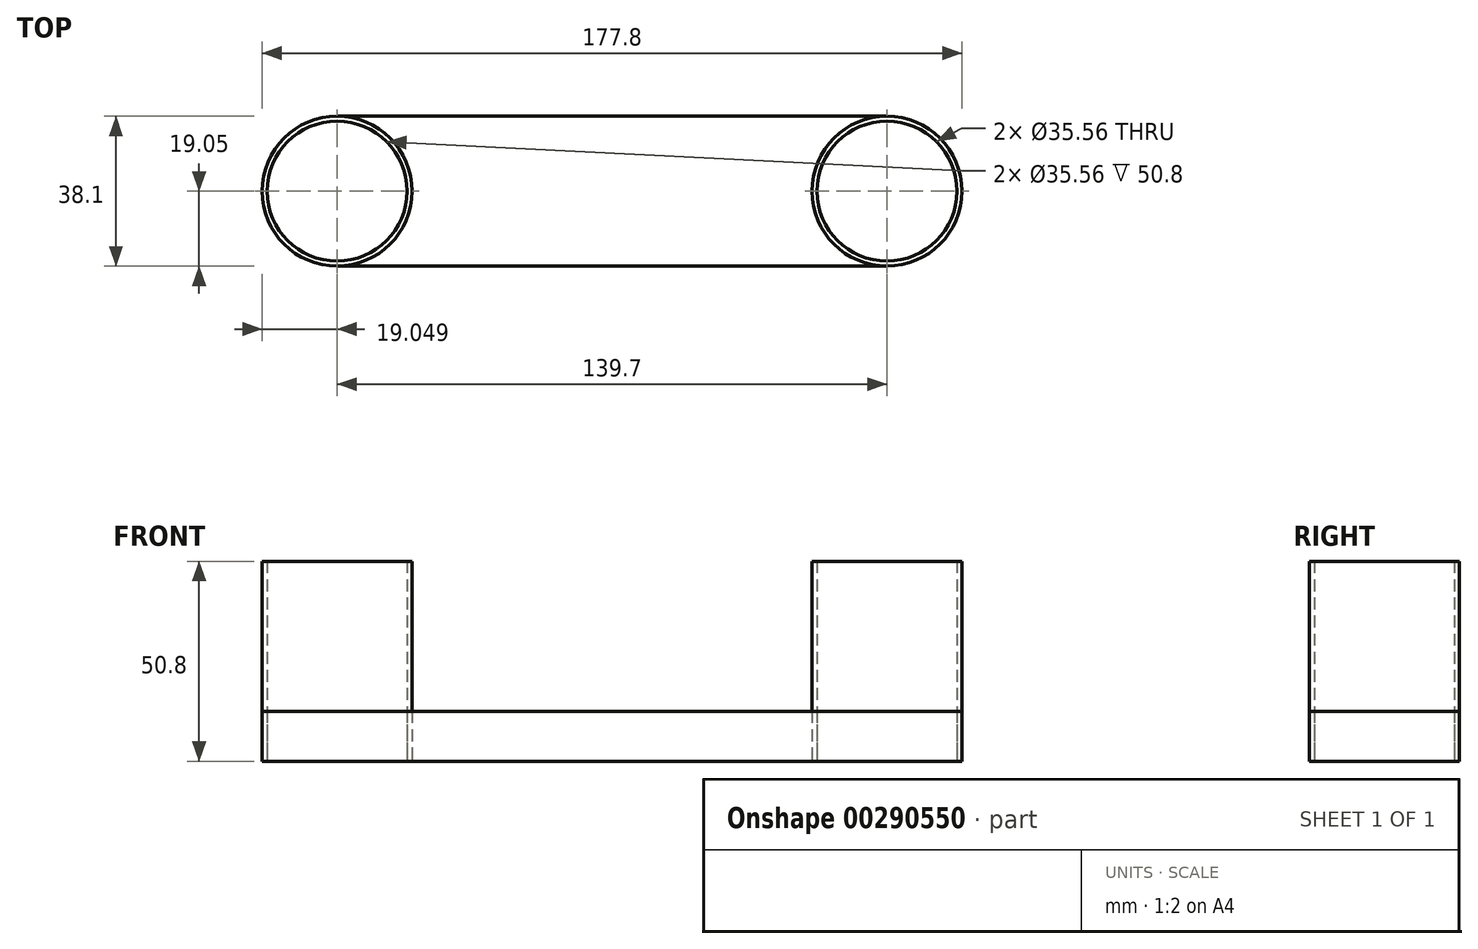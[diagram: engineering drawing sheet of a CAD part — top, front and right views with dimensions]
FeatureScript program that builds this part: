
annotation { "Feature Type Name" : "Feature", "Feature Type Description" : "" }
export const myFeature = defineFeature(function(context is Context, id is Id, definition is map)
    precondition{}
    {
        {
            var Q0;
            Q0=qCreatedBy(makeId("Top.planeOp"),FACE);
            var sketch = newSketch(context, id + "F0", { "sketchPlane" : qUnion([Q0])});
            skLineSegment(sketch, "E0", {"start": v(-93.86, 0) * mm, "end": v(0, 0) * mm, "construction": true});
            skLineSegment(sketch, "E1", {"start": v(0, 0) * mm, "end": v(83.94, 0) * mm, "construction": true});
            skLineSegment(sketch, "E2", {"start": v(83.94, 0) * mm, "end": v(83.94, 17.46) * mm, "construction": true});
            skLineSegment(sketch, "E3", {"start": v(83.94, 17.46) * mm, "end": v(45.84, 17.46) * mm, "construction": true});
            skLineSegment(sketch, "E4", {"start": v(45.84, 17.46) * mm, "end": v(45.84, 0) * mm, "construction": true});
            skLineSegment(sketch, "E5", {"start": v(45.84, 0) * mm, "end": v(-55.76, 0) * mm, "construction": true});
            skLineSegment(sketch, "E6", {"start": v(-55.76, 0) * mm, "end": v(-55.76, 17.78) * mm, "construction": true});
            skLineSegment(sketch, "E7", {"start": v(-55.76, 17.78) * mm, "end": v(-93.86, 17.78) * mm, "construction": true});
            skLineSegment(sketch, "E8", {"start": v(-93.86, 17.78) * mm, "end": v(-93.86, 0) * mm, "construction": true});
            skLineSegment(sketch, "E9", {"start": v(-93.86, 0) * mm, "end": v(-74.81, 17.78) * mm, "construction": true});
            skLineSegment(sketch, "E10", {"start": v(-74.81, 17.78) * mm, "end": v(-74.81, 0) * mm, "construction": true});
            skCircle(sketch, "E11", {"center": v(-74.81, 0) * mm, "radius": 19.05 * mm});
            skCircle(sketch, "E12", {"center": v(64.89, 0) * mm, "radius": 19.05 * mm});
            skLineSegment(sketch, "E13", {"start": v(-74.81, 19.05) * mm, "end": v(64.89, 19.05) * mm});
            skLineSegment(sketch, "E14", {"start": v(-74.81, -19.05) * mm, "end": v(64.89, -19.05) * mm});
            skCircle(sketch, "E15", {"center": v(-74.81, 0) * mm, "radius": 17.78 * mm});
            skCircle(sketch, "E16", {"center": v(64.89, 0) * mm, "radius": 17.78 * mm});
            skSolve(sketch);
        }
        {
            var Q0;
            {var subQ0=sQuery(id+"F0.wireOp",EDGE,"E11");var subQ1=makeQuery(id+"F0.imprint","INTERSECT",VERTEX,{"derivedFrom":[subQ0,sQuery(id+"F0.wireOp",EDGE,"E13")]});Q0=makeQuery(id+"F0.imprint","IMPRINT",FACE,{"disambiguationData":[TD([[makeQuery(id+"F0.imprint","IMPRINT",EDGE,{"disambiguationData":[TD([[subQ1,-1.0]])],"derivedFrom":subQ0}),1.0]])]});}
            var Q1;
            {var subQ0=sQuery(id+"F0.wireOp",EDGE,"E12");var subQ1=makeQuery(id+"F0.imprint","INTERSECT",VERTEX,{"derivedFrom":[subQ0,sQuery(id+"F0.wireOp",EDGE,"E13")]});Q1=makeQuery(id+"F0.imprint","IMPRINT",FACE,{"disambiguationData":[TD([[makeQuery(id+"F0.imprint","IMPRINT",EDGE,{"disambiguationData":[TD([[subQ1,-1.0]])],"derivedFrom":subQ0}),1.0]])]});}
            extrude(context, id + "F1", {"entities" : qUnion([Q0, Q1]), "depth" : 50.8 * mm});
        }
        {
            var Q0;
            Q0 = qSketchRegion(id + "F0", true);
            extrude(context, id + "F2", {"entities" : qUnion([Q0]), "depth" : 12.7 * mm});
        }
    });
